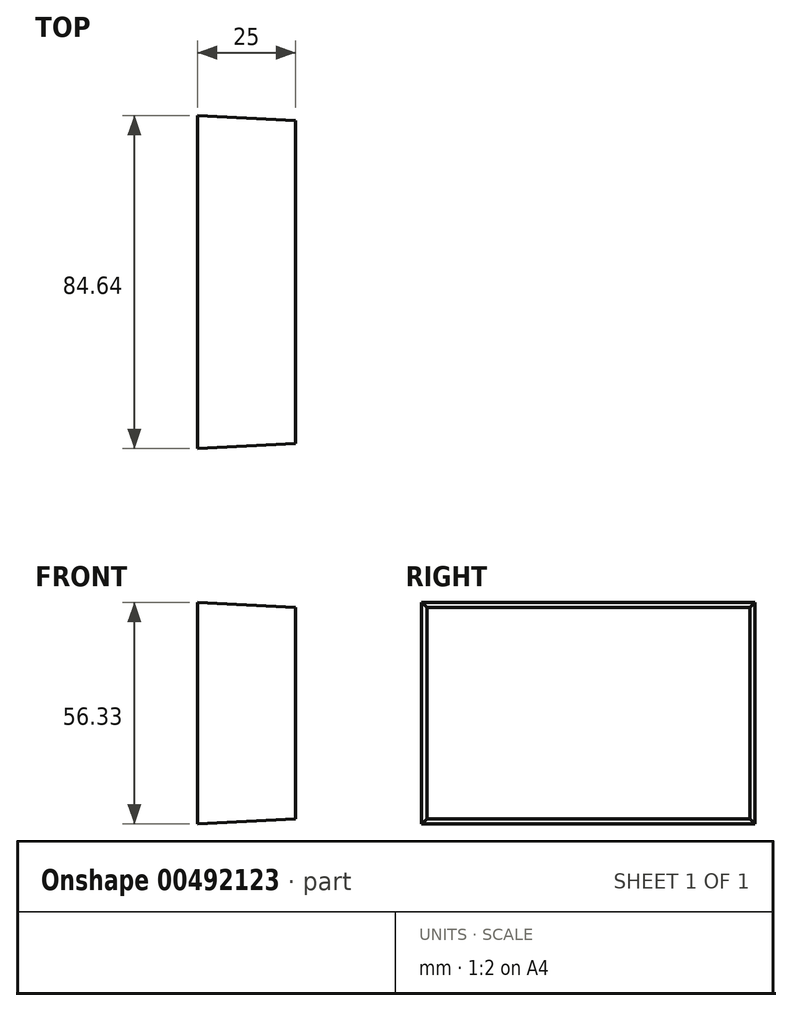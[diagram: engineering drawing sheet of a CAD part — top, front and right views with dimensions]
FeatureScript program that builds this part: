
annotation { "Feature Type Name" : "Feature", "Feature Type Description" : "" }
export const myFeature = defineFeature(function(context is Context, id is Id, definition is map)
    precondition{}
    {
        {
            var Q0;
            Q0=qCreatedBy(makeId("Right.planeOp"),FACE);
            var sketch = newSketch(context, id + "F0", { "sketchPlane" : qUnion([Q0])});
            skLineSegment(sketch, "E0.bottom", {"start": v(-52.67, 32.68) * mm, "end": v(29.35, 32.68) * mm});
            skLineSegment(sketch, "E0.top", {"start": v(-52.67, -21.03) * mm, "end": v(29.35, -21.03) * mm});
            skLineSegment(sketch, "E0.left", {"start": v(-52.67, 32.68) * mm, "end": v(-52.67, -21.03) * mm});
            skLineSegment(sketch, "E0.right", {"start": v(29.35, 32.68) * mm, "end": v(29.35, -21.03) * mm});
            skSolve(sketch);
        }
        {
            var Q0;
            Q0=makeQuery(id+"F0.imprint","IMPRINT",FACE,{"disambiguationData":[TD([[makeQuery(id+"F0.imprint","IMPRINT",EDGE,{"derivedFrom":sQuery(id+"F0.wireOp",EDGE,"E0.bottom")}),-1.0]])]});
            extrude(context, id + "F1", {"entities" : qUnion([Q0]), "oppositeDirection" : true, "depth" : 25 * mm, "offsetDistance" : 25 * mm, "hasDraft" : true, "draftAngle" : 3 * degree});
        }
    });
